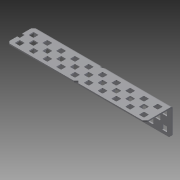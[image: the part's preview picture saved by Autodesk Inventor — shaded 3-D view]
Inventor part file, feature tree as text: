
AUTODESK INVENTOR PART (.ipt)
format: ipt  version: 2014 (Build 180170000, 170)  size: 977,408 bytes
history: native  units: in
note: dims shown in document units (in); Inventor stores cm internally (conversion verified against a paired STEP export)
features: other x1, imported_body x1, extrude x1, sketch x1
ambient origin geometry x8: Origin, YZ Plane, XZ Plane, XY Plane, X Axis, Y Axis, Z Axis, Center Point
bodies: Body1 (feature_tree)
feature tree (4):
  parser-record x1  (decoder bookkeeping rows leaked as tree rows — omitted from the tree; the rows remain in map.json)
  imported_body  "Base1"
  extrude  "Extrusion1"  [1 undecoded]
  sketch  "Sketch1"  dims[d0=1.0in d1=0.0in]
note: 1 required parameter value undecoded (feature->parameter linkage not recoverable at this tier; creation-order binding heuristic only, values carry confidence <= 0.55)
